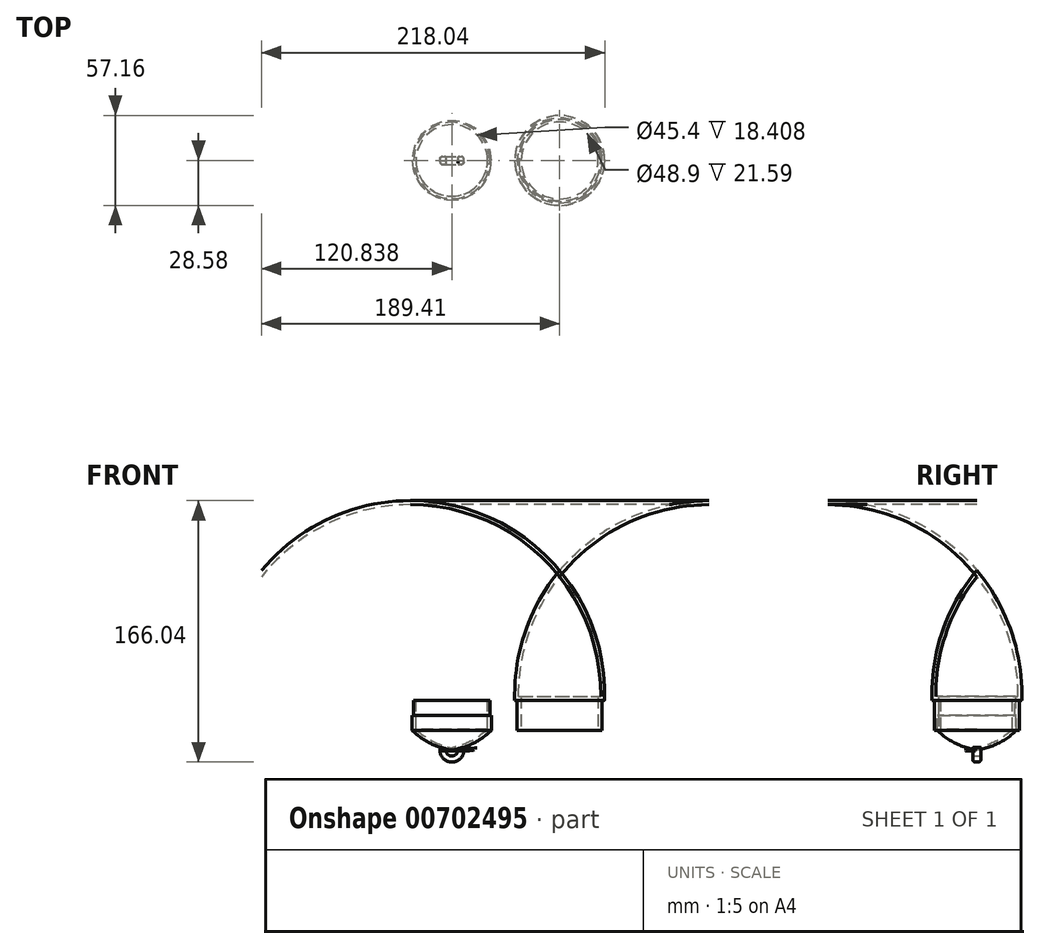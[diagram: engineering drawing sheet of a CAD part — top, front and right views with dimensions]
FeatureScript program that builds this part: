
annotation { "Feature Type Name" : "Feature", "Feature Type Description" : "" }
export const myFeature = defineFeature(function(context is Context, id is Id, definition is map)
    precondition{}
    {
        {
            var Q0;
            Q0=qCreatedBy(makeId("Front.planeOp"),FACE);
            var sketch = newSketch(context, id + "F0", { "sketchPlane" : qUnion([Q0])});
            skLineSegment(sketch, "E0", {"start": v(0, 0) * mm, "end": v(0, 101.6) * mm});
            skLineSegment(sketch, "E1", {"start": v(0, 0) * mm, "end": v(26.99, 0) * mm});
            skLineSegment(sketch, "E2", {"start": v(26.99, 0) * mm, "end": v(26.99, 19.05) * mm});
            skLineSegment(sketch, "E3", {"start": v(26.99, 19.05) * mm, "end": v(28.57, 19.05) * mm});
            skArc(sketch, "E4", {"start": v(28.57, 19.05) * mm, "mid": v(21.84, 62.94) * mm, "end": v(0, 101.6) * mm});
            skArc(sketch, "E5.0", {"start": v(26.08, 21.59) * mm, "mid": v(19.54, 61.81) * mm, "end": v(0, 97.57) * mm});
            skLineSegment(sketch, "E5.1", {"start": v(24.45, 21.59) * mm, "end": v(26.08, 21.59) * mm});
            skLineSegment(sketch, "E5.2", {"start": v(24.45, 0) * mm, "end": v(24.45, 21.59) * mm});
            skSolve(sketch);
        }
        {
            var Q0;
            {var subQ0=sQuery(id+"F0.wireOp",EDGE,"E2");Q0=makeQuery(id+"F0.imprint","IMPRINT",FACE,{"disambiguationData":[TD([[makeQuery(id+"F0.imprint","IMPRINT",EDGE,{"derivedFrom":subQ0}),1.0]])]});}
            var Q1;
            Q1=sQuery(id+"F0.wireOp",EDGE,"E0");
            revolve(context, id + "F1", {"surfaceOperationType" : NewSurfaceOperationType.NEW, "entities" : qUnion([Q0]), "axis" : qUnion([Q1]), "revolveType" : RevolveType.FULL});
        }
        {
            var Q0;
            Q0=qCreatedBy(makeId("Front.planeOp"),FACE);
            var sketch = newSketch(context, id + "F2", { "sketchPlane" : qUnion([Q0])});
            skLineSegment(sketch, "E6", {"start": v(-68.57, 19.2) * mm, "end": v(-68.57, -12.54) * mm});
            skLineSegment(sketch, "E7", {"start": v(-92.8, 19.05) * mm, "end": v(-92.8, 9.53) * mm});
            skArc(sketch, "E8.0", {"start": v(-91.27, 0.64) * mm, "mid": v(-80.78, -6.85) * mm, "end": v(-68.57, -11) * mm});
            skLineSegment(sketch, "E8.1", {"start": v(-91.27, 19.05) * mm, "end": v(-91.27, 0.64) * mm});
            skLineSegment(sketch, "E9", {"start": v(-92.8, 19.05) * mm, "end": v(-91.27, 19.05) * mm});
            skPoint(sketch, "E10.end.orphan", {"position": v(-92.8, 0) * mm});
            skLineSegment(sketch, "E11", {"start": v(-92.8, 9.53) * mm, "end": v(-93.69, 9.53) * mm});
            skLineSegment(sketch, "E12", {"start": v(-93.69, 9.53) * mm, "end": v(-93.69, 0) * mm});
            skArc(sketch, "E13", {"start": v(-93.69, 0) * mm, "mid": v(-82.1, -8.23) * mm, "end": v(-68.57, -12.54) * mm});
            skSolve(sketch);
        }
        {
            var Q0;
            Q0=makeQuery(id+"F2.imprint","IMPRINT",FACE,{"disambiguationData":[TD([[makeQuery(id+"F2.imprint","IMPRINT",EDGE,{"derivedFrom":sQuery(id+"F2.wireOp",EDGE,"E6")}),-1.0]])]});
            var Q1;
            Q1=sQuery(id+"F2.wireOp",EDGE,"E6");
            revolve(context, id + "F3", {"surfaceOperationType" : NewSurfaceOperationType.NEW, "entities" : qUnion([Q0]), "axis" : qUnion([Q1]), "revolveType" : RevolveType.FULL});
        }
        {
            var Q0;
            Q0=qCreatedBy(makeId("Front.planeOp"),FACE);
            var sketch = newSketch(context, id + "F4", { "sketchPlane" : qUnion([Q0])});
            skArc(sketch, "E14", {"start": v(-75.78, -10.24) * mm, "mid": v(-68.38, -20.11) * mm, "end": v(-61.3, -10) * mm});
            skArc(sketch, "E15", {"start": v(-72.17, -11.46) * mm, "mid": v(-68.44, -16.3) * mm, "end": v(-64.87, -11.35) * mm});
            skLineSegment(sketch, "E16", {"start": v(-75.78, -10.24) * mm, "end": v(-72.17, -11.46) * mm});
            skLineSegment(sketch, "E17", {"start": v(-64.87, -11.35) * mm, "end": v(-61.3, -10) * mm});
            skSolve(sketch);
        }
        {
            var Q0;
            Q0=makeQuery(id+"F4.imprint","IMPRINT",FACE,{"disambiguationData":[TD([[makeQuery(id+"F4.imprint","IMPRINT",EDGE,{"derivedFrom":sQuery(id+"F4.wireOp",EDGE,"E14")}),1.0]])]});
            extrude(context, id + "F5", {"entities" : qUnion([Q0]), "operationType" : NewBodyOperationType.ADD, "depth" : 2.54 * mm, "offsetDistance" : 25.4 * mm});
        }
        {
            var Q0;
            Q0=makeQuery(id+"F5.opExtrude","CAP_FACE",FACE,{"disambiguationData":[OSD([sQuery(id+"F4.wireOp",EDGE,"E14"),sQuery(id+"F4.wireOp",EDGE,"E15"),sQuery(id+"F4.wireOp",EDGE,"E16"),sQuery(id+"F4.wireOp",EDGE,"E17")])],"isStart":true});
            extrude(context, id + "F6", {"entities" : qUnion([Q0]), "operationType" : NewBodyOperationType.ADD, "depth" : 2.54 * mm, "offsetDistance" : 25.4 * mm});
        }
        {
            var Q0;
            Q0=makeQuery(id+"F6.opExtrude","CAP_EDGE",EDGE,{"disambiguationData":[OSD([sQuery(id+"F4.wireOp",EDGE,"E14")])],"isStart":false});
            fillet(context, id + "F7", {"entities" : qUnion([Q0]), "radius" : 1.52 * mm, "tangentPropagation" : true, "allowEdgeOverflow" : false});
        }
        {
            var Q0;
            Q0=makeQuery(id+"F5.opExtrude","CAP_EDGE",EDGE,{"disambiguationData":[OSD([sQuery(id+"F4.wireOp",EDGE,"E14")])],"isStart":false});
            fillet(context, id + "F8", {"entities" : qUnion([Q0]), "radius" : 1.52 * mm, "tangentPropagation" : true, "allowEdgeOverflow" : false});
        }
        {
            var Q0;
            Q0=makeQuery(id+"F5.opExtrude","CAP_EDGE",EDGE,{"disambiguationData":[OSD([sQuery(id+"F4.wireOp",EDGE,"E15")])],"isStart":false});
            fillet(context, id + "F9", {"entities" : qUnion([Q0]), "radius" : 1.02 * mm, "tangentPropagation" : true, "allowEdgeOverflow" : false});
        }
        {
            var Q0;
            Q0=makeQuery(id+"F6.opExtrude","CAP_EDGE",EDGE,{"disambiguationData":[OSD([sQuery(id+"F4.wireOp",EDGE,"E15")])],"isStart":false});
            fillet(context, id + "F10", {"entities" : qUnion([Q0]), "radius" : 1.02 * mm, "tangentPropagation" : true, "allowEdgeOverflow" : false});
        }
    });
